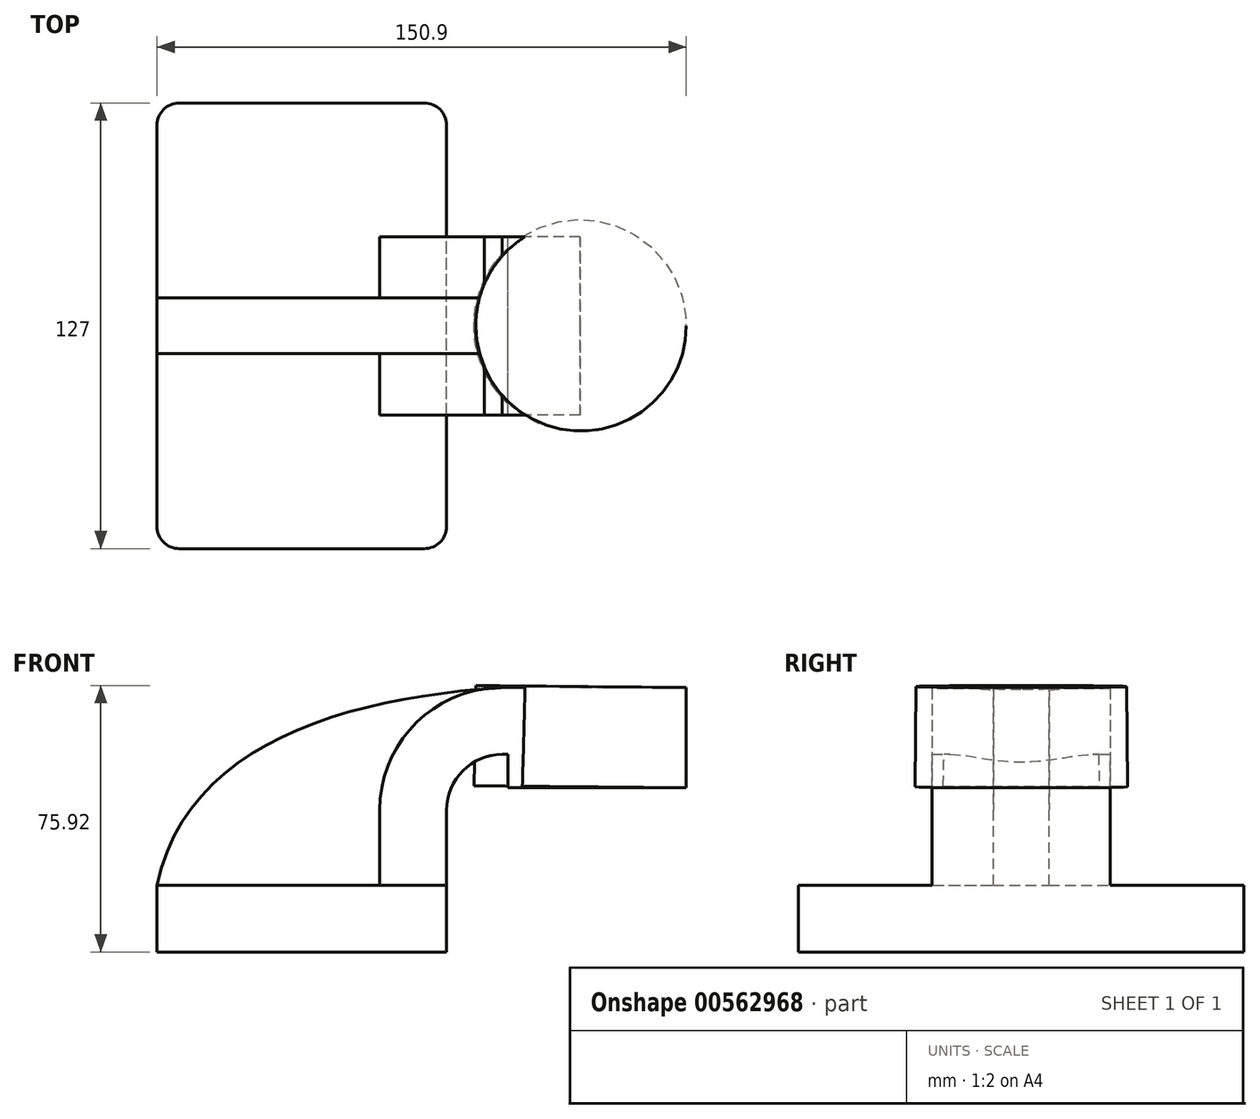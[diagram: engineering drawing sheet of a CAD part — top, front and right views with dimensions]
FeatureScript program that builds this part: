
annotation { "Feature Type Name" : "Feature", "Feature Type Description" : "" }
export const myFeature = defineFeature(function(context is Context, id is Id, definition is map)
    precondition{}
    {
        {
            var Q0;
            Q0=qCreatedBy(makeId("Front.planeOp"),FACE);
            var sketch = newSketch(context, id + "F0", { "sketchPlane" : qUnion([Q0])});
            skLineSegment(sketch, "E0.bottom", {"start": v(-41.28, 9.52) * mm, "end": v(41.28, 9.53) * mm});
            skLineSegment(sketch, "E0.top", {"start": v(-41.28, -9.53) * mm, "end": v(41.28, -9.53) * mm});
            skLineSegment(sketch, "E0.left", {"start": v(-41.28, 9.52) * mm, "end": v(-41.28, -9.53) * mm});
            skLineSegment(sketch, "E0.right", {"start": v(41.28, 9.53) * mm, "end": v(41.28, -9.52) * mm});
            skPoint(sketch, "E0.middle", {"position": v(0, 0) * mm});
            skLineSegment(sketch, "E1.bottom", {"start": v(109.62, 37.24) * mm, "end": v(58.82, 37.24) * mm});
            skLineSegment(sketch, "E1.top", {"start": v(109.62, 65.81) * mm, "end": v(58.82, 65.81) * mm});
            skLineSegment(sketch, "E1.left", {"start": v(109.62, 37.24) * mm, "end": v(109.62, 65.81) * mm});
            skLineSegment(sketch, "E1.right", {"start": v(58.82, 37.24) * mm, "end": v(58.82, 65.81) * mm});
            skPoint(sketch, "E1.middle", {"position": v(84.22, 51.53) * mm});
            skLineSegment(sketch, "E2", {"start": v(41.27, 9.53) * mm, "end": v(41.27, 30.89) * mm});
            skArc(sketch, "E3", {"start": v(41.27, 30.89) * mm, "mid": v(45.92, 42.11) * mm, "end": v(57.15, 46.76) * mm});
            skLineSegment(sketch, "E4", {"start": v(57.15, 46.76) * mm, "end": v(79.25, 46.76) * mm});
            skLineSegment(sketch, "E5.0", {"start": v(57.15, 65.81) * mm, "end": v(79.62, 65.81) * mm});
            skArc(sketch, "E5.1", {"start": v(22.23, 30.89) * mm, "mid": v(32.45, 55.58) * mm, "end": v(57.15, 65.81) * mm});
            skLineSegment(sketch, "E5.2", {"start": v(22.22, 9.53) * mm, "end": v(22.22, 30.89) * mm});
            skLineSegment(sketch, "E6", {"start": v(79.35, 37.24) * mm, "end": v(79.62, 65.81) * mm});
            skFitSpline(sketch, "E7", {"points": [v(-41.28, 9.52) * mm, v(57.15, 65.81) * mm], "startDerivative": vector(25.28, 121.97) * mm, "endDerivative": vector(131.85, 8.51) * mm});
            skSolve(sketch);
        }
        {
            var Q0;
            Q0=makeQuery(id+"F0.imprint","IMPRINT",FACE,{"disambiguationData":[TD([[makeQuery(id+"F0.imprint","IMPRINT",EDGE,{"derivedFrom":sQuery(id+"F0.wireOp",EDGE,"E0.top")}),1.0]])]});
            extrude(context, id + "F1", {"entities" : qUnion([Q0]), "endBound" : BoundingType.SYMMETRIC, "depth" : 127 * mm, "offsetDistance" : 25.4 * mm});
        }
        {
            var Q0;
            {var subQ1=sQuery(id+"F0.wireOp",EDGE,"E2");Q0=makeQuery(id+"F0.imprint","IMPRINT",FACE,{"disambiguationData":[TD([[makeQuery(id+"F0.imprint","IMPRINT",EDGE,{"derivedFrom":subQ1}),1.0]])]});}
            var Q1;
            {var subQ6=sQuery(id+"F0.wireOp",EDGE,"E6");Q1=makeQuery(id+"F0.imprint","IMPRINT",FACE,{"disambiguationData":[TD([[makeQuery(id+"F0.imprint","IMPRINT",EDGE,{"derivedFrom":subQ6}),1.0]])]});}
            extrude(context, id + "F2", {"entities" : qUnion([Q0, Q1]), "operationType" : NewBodyOperationType.ADD, "endBound" : BoundingType.SYMMETRIC, "depth" : 50.8 * mm, "offsetDistance" : 25.4 * mm});
        }
        {
            var Q0;
            {var subQ3=sQuery(id+"F0.wireOp",EDGE,"E5.2");Q0=makeQuery(id+"F0.imprint","IMPRINT",FACE,{"disambiguationData":[TD([[makeQuery(id+"F0.imprint","IMPRINT",EDGE,{"derivedFrom":subQ3}),1.0]])]});}
            extrude(context, id + "F3", {"entities" : qUnion([Q0]), "operationType" : NewBodyOperationType.ADD, "endBound" : BoundingType.SYMMETRIC, "depth" : 15.88 * mm, "offsetDistance" : 25.4 * mm});
        }
        {
            var Q0;
            Q0=makeQuery(id+"F0.imprint","IMPRINT",FACE,{"disambiguationData":[TD([[makeQuery(id+"F0.imprint","IMPRINT",EDGE,{"derivedFrom":sQuery(id+"F0.wireOp",EDGE,"E1.top")}),1.0]])]});
            var Q1;
            Q1=sQuery(id+"F0.wireOp",EDGE,"E6");
            revolve(context, id + "F4", {"operationType" : NewBodyOperationType.ADD, "entities" : qUnion([Q0]), "axis" : qUnion([Q1]), "revolveType" : RevolveType.FULL});
        }
        {
            var Q0;
            Q0=makeQuery(id+"F1.opExtrude","CAP_EDGE",EDGE,{"disambiguationData":[OSD([sQuery(id+"F0.wireOp",EDGE,"E0.left")])],"isStart":false});
            var Q1;
            Q1=makeQuery(id+"F1.opExtrude","CAP_EDGE",EDGE,{"disambiguationData":[OSD([sQuery(id+"F0.wireOp",EDGE,"E0.right")])],"isStart":false});
            var Q2;
            Q2=makeQuery(id+"F1.opExtrude","CAP_EDGE",EDGE,{"disambiguationData":[OSD([sQuery(id+"F0.wireOp",EDGE,"E0.right")])],"isStart":true});
            var Q3;
            Q3=makeQuery(id+"F1.opExtrude","CAP_EDGE",EDGE,{"disambiguationData":[OSD([sQuery(id+"F0.wireOp",EDGE,"E0.left")])],"isStart":true});
            fillet(context, id + "F5", {"entities" : qUnion([Q0, Q1, Q2, Q3]), "radius" : 6.35 * mm, "tangentPropagation" : true, "allowEdgeOverflow" : false});
        }
    });
